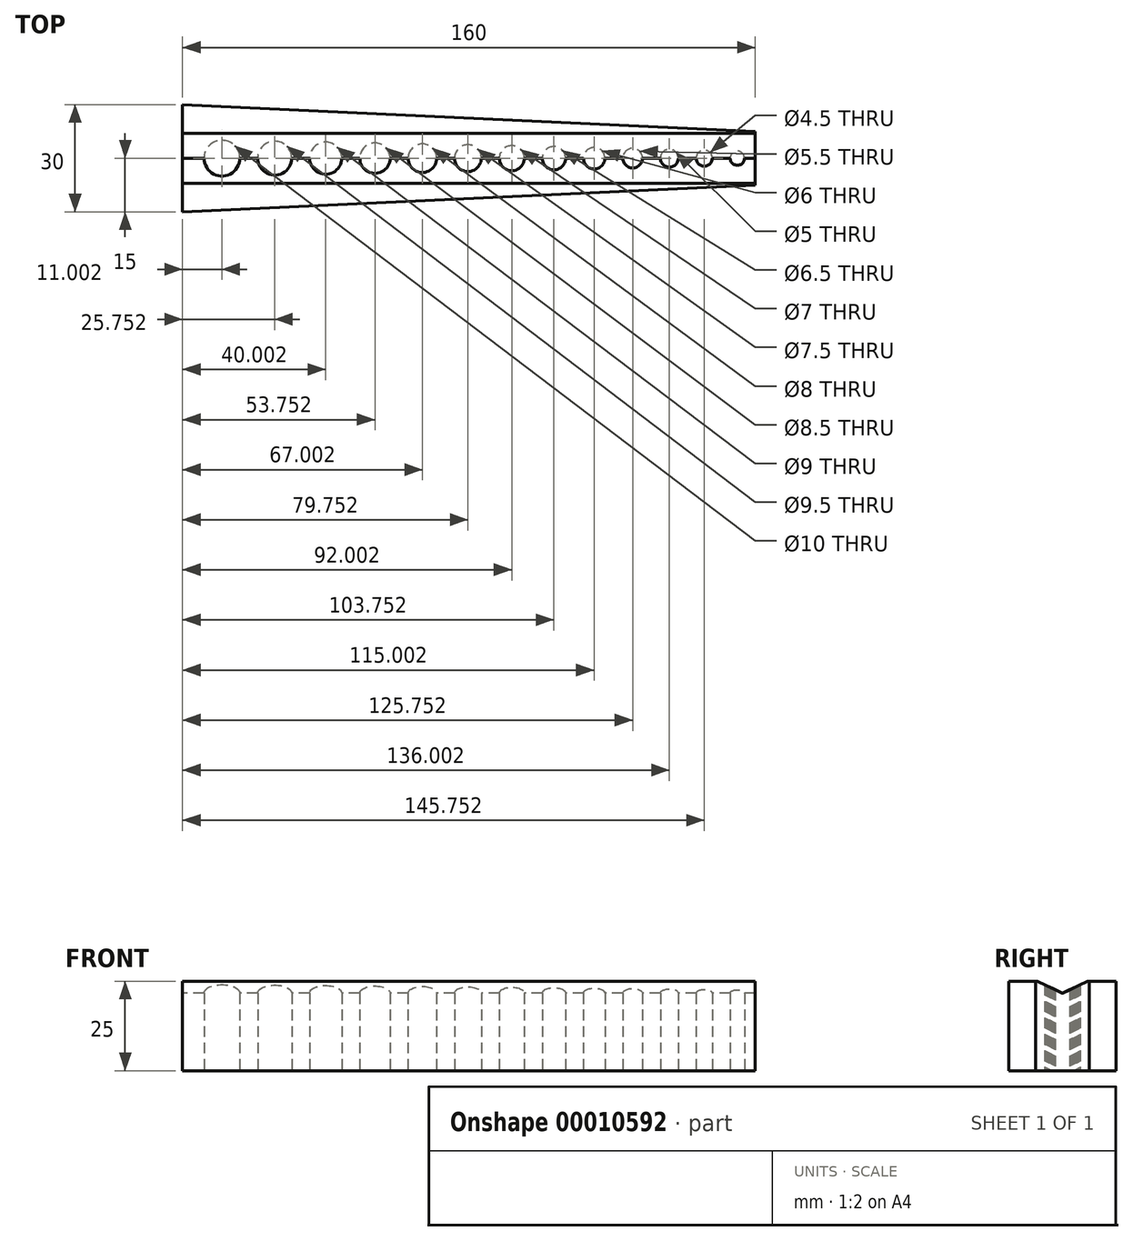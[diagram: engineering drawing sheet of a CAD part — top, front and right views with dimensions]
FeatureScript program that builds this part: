
annotation { "Feature Type Name" : "Feature", "Feature Type Description" : "" }
export const myFeature = defineFeature(function(context is Context, id is Id, definition is map)
    precondition{}
    {
        {
            var Q0;
            Q0=qCreatedBy(makeId("Top.planeOp"),FACE);
            var sketch = newSketch(context, id + "F0", { "sketchPlane" : qUnion([Q0])});
            skLineSegment(sketch, "E0.rect.left", {"start": v(97.16, 7.5) * mm, "end": v(97.16, -7.5) * mm});
            skLineSegment(sketch, "E0.rect.right", {"start": v(-62.84, 15) * mm, "end": v(-62.84, -15) * mm});
            skPoint(sketch, "E0.rect.middle", {"position": v(0, 0) * mm});
            skLineSegment(sketch, "E1", {"start": v(-62.84, 15) * mm, "end": v(97.16, 7.5) * mm});
            skLineSegment(sketch, "E2", {"start": v(-62.84, -15) * mm, "end": v(97.16, -7.5) * mm});
            skLineSegment(sketch, "E3.0", {"start": v(-51.84, 15) * mm, "end": v(-51.84, -15) * mm, "construction": true});
            skLineSegment(sketch, "E4.0", {"start": v(-37.09, 15) * mm, "end": v(-37.09, -15) * mm, "construction": true});
            skLineSegment(sketch, "E5.0", {"start": v(-22.84, 15) * mm, "end": v(-22.84, -15) * mm, "construction": true});
            skLineSegment(sketch, "E6.0", {"start": v(-9.09, 15) * mm, "end": v(-9.09, -15) * mm, "construction": true});
            skLineSegment(sketch, "E7.0", {"start": v(4.16, 15) * mm, "end": v(4.16, -15) * mm, "construction": true});
            skLineSegment(sketch, "E8.0", {"start": v(16.91, 15) * mm, "end": v(16.91, -15) * mm, "construction": true});
            skLineSegment(sketch, "E9.0", {"start": v(29.16, 15) * mm, "end": v(29.16, -15) * mm, "construction": true});
            skLineSegment(sketch, "E10.0", {"start": v(40.91, 15) * mm, "end": v(40.91, -15) * mm, "construction": true});
            skLineSegment(sketch, "E11.0", {"start": v(73.16, 15) * mm, "end": v(73.16, -15) * mm, "construction": true});
            skCircle(sketch, "E12", {"center": v(-51.84, 0) * mm, "radius": 5 * mm});
            skCircle(sketch, "E13", {"center": v(-37.09, 0) * mm, "radius": 4.75 * mm});
            skCircle(sketch, "E14", {"center": v(-22.84, 0) * mm, "radius": 4.5 * mm});
            skCircle(sketch, "E15", {"center": v(-9.09, 0) * mm, "radius": 4.25 * mm});
            skCircle(sketch, "E16", {"center": v(4.16, 0) * mm, "radius": 4 * mm});
            skCircle(sketch, "E17", {"center": v(16.91, 0) * mm, "radius": 3.75 * mm});
            skCircle(sketch, "E18", {"center": v(29.16, 0) * mm, "radius": 3.5 * mm});
            skCircle(sketch, "E19", {"center": v(40.91, 0) * mm, "radius": 3.25 * mm});
            skCircle(sketch, "E20", {"center": v(73.16, 0) * mm, "radius": 2.5 * mm});
            skLineSegment(sketch, "E21.0", {"start": v(52.16, 15) * mm, "end": v(52.16, -15) * mm, "construction": true});
            skLineSegment(sketch, "E22.0", {"start": v(62.91, 15) * mm, "end": v(62.91, -15) * mm, "construction": true});
            skCircle(sketch, "E23", {"center": v(52.16, 0) * mm, "radius": 3 * mm});
            skCircle(sketch, "E24", {"center": v(62.91, 0) * mm, "radius": 2.75 * mm});
            skLineSegment(sketch, "E25.0", {"start": v(82.91, 15) * mm, "end": v(82.91, -15) * mm, "construction": true});
            skCircle(sketch, "E26", {"center": v(82.91, 0) * mm, "radius": 2.25 * mm});
            skLineSegment(sketch, "E27.0", {"start": v(92.16, 15) * mm, "end": v(92.16, -15) * mm, "construction": true});
            skCircle(sketch, "E28", {"center": v(92.16, 0) * mm, "radius": 2 * mm});
            skSolve(sketch);
        }
        {
            var Q0;
            Q0 = qSketchRegion(id + "F0", true);
            extrude(context, id + "F1", {"entities" : qUnion([Q0]), "depth" : 25 * mm});
        }
        {
            var Q0;
            Q0=makeQuery(id+"F1.opExtrude","SWEPT_FACE",FACE,{"disambiguationData":[OSD([sQuery(id+"F0.wireOp",EDGE,"E0.rect.right")])]});
            var sketch = newSketch(context, id + "F2", { "sketchPlane" : qUnion([Q0])});
            skLineSegment(sketch, "E29", {"start": v(-7, 25) * mm, "end": v(0, 21.65) * mm});
            skLineSegment(sketch, "E30", {"start": v(7, 25) * mm, "end": v(0, 21.65) * mm});
            skSolve(sketch);
        }
        {
            var Q0;
            {var subQ2=sQuery(id+"F2.wireOp",EDGE,"E29");Q0=makeQuery(id+"F2.imprint","IMPRINT",FACE,{"disambiguationData":[TD([[makeQuery(id+"F2.imprint","IMPRINT",EDGE,{"derivedFrom":subQ2}),1.0]])]});}
            var Q1;
            Q1=sQuery(id+"F2.wireOp",EDGE,"E29");
            var Q2;
            Q2=sQuery(id+"F2.wireOp",EDGE,"E30");
            extrude(context, id + "F3", {"entities" : qUnion([Q0]), "operationType" : NewBodyOperationType.REMOVE, "surfaceEntities" : qUnion([Q1, Q2]), "endBound" : BoundingType.THROUGH_ALL, "oppositeDirection" : true, "depth" : 25 * mm});
        }
    });
